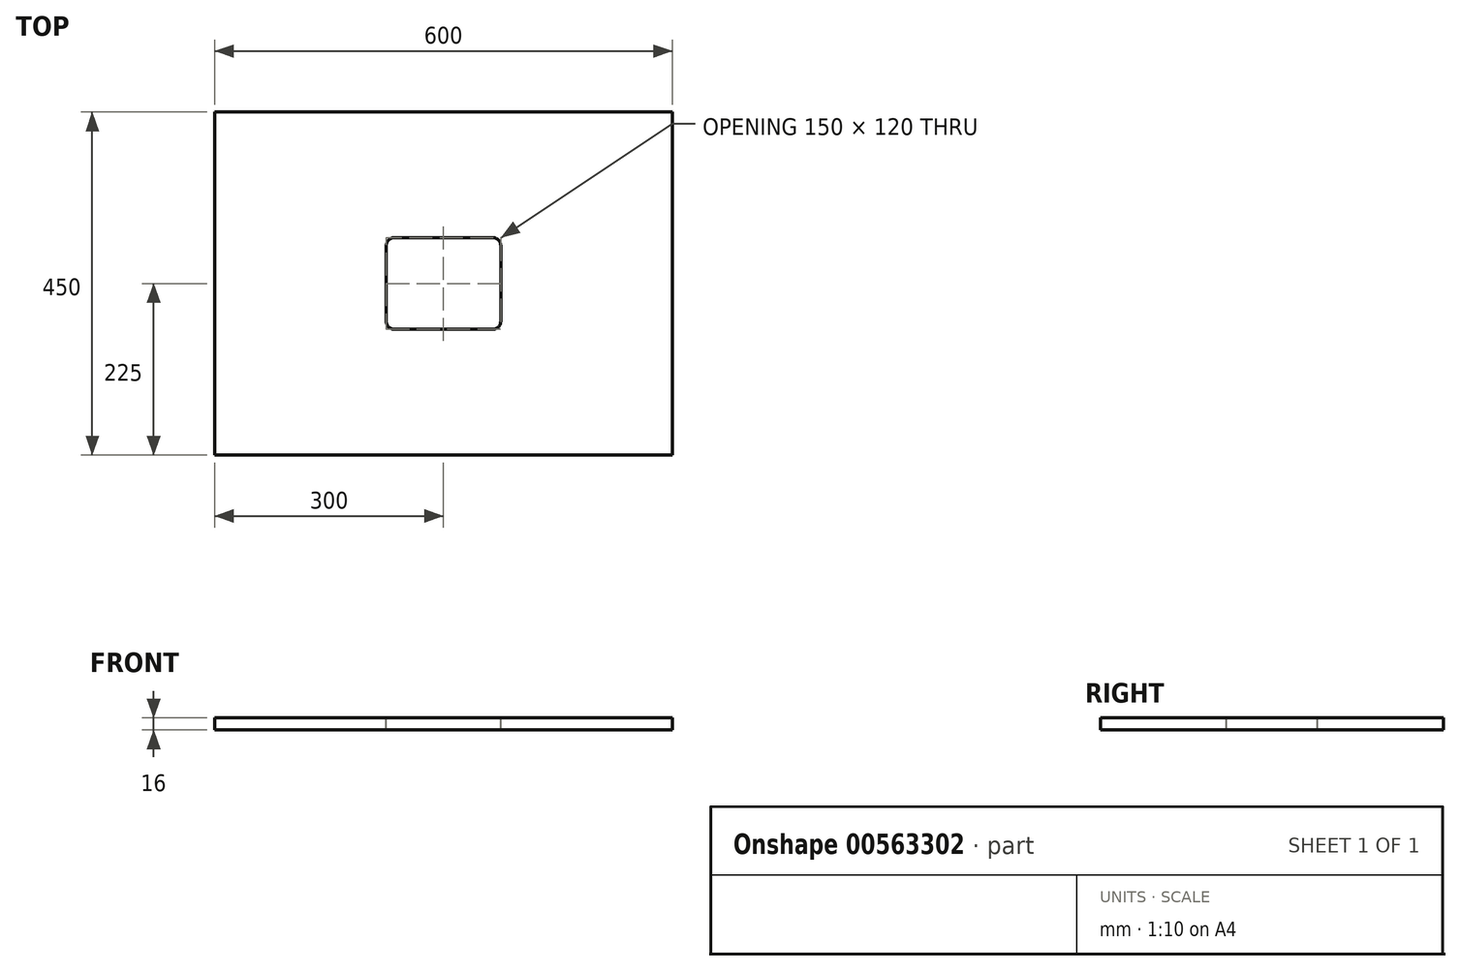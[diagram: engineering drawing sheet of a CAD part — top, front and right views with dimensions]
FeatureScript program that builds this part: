
annotation { "Feature Type Name" : "Feature", "Feature Type Description" : "" }
export const myFeature = defineFeature(function(context is Context, id is Id, definition is map)
    precondition{}
    {
        {
            var Q0;
            Q0=qCreatedBy(makeId("Top.planeOp"),FACE);
            var sketch = newSketch(context, id + "F0", { "sketchPlane" : qUnion([Q0])});
            skLineSegment(sketch, "E0.bottom", {"start": v(300, 225) * mm, "end": v(-300, 225) * mm});
            skLineSegment(sketch, "E0.top", {"start": v(300, -225) * mm, "end": v(-300, -225) * mm});
            skLineSegment(sketch, "E0.left", {"start": v(300, 225) * mm, "end": v(300, -225) * mm});
            skLineSegment(sketch, "E0.right", {"start": v(-300, 225) * mm, "end": v(-300, -225) * mm});
            skPoint(sketch, "E0.middle", {"position": v(0, 0) * mm});
            skSolve(sketch);
        }
        {
            var Q0;
            Q0=makeQuery(id+"F0.imprint","IMPRINT",FACE,{"disambiguationData":[TD([[makeQuery(id+"F0.imprint","IMPRINT",EDGE,{"derivedFrom":sQuery(id+"F0.wireOp",EDGE,"E0.bottom")}),1.0]])]});
            extrude(context, id + "F1", {"entities" : qUnion([Q0]), "depth" : 16 * mm, "offsetDistance" : 25 * mm});
        }
        {
            var Q0;
            Q0=makeQuery(id+"F1.opExtrude","CAP_FACE",FACE,{"disambiguationData":[OSD([sQuery(id+"F0.wireOp",EDGE,"E0.bottom"),sQuery(id+"F0.wireOp",EDGE,"E0.top"),sQuery(id+"F0.wireOp",EDGE,"E0.left"),sQuery(id+"F0.wireOp",EDGE,"E0.right")])],"isStart":false});
            var sketch = newSketch(context, id + "F2", { "sketchPlane" : qUnion([Q0])});
            skLineSegment(sketch, "E1.bottom", {"start": v(75, 60) * mm, "end": v(-75, 60) * mm});
            skLineSegment(sketch, "E1.top", {"start": v(75, -60) * mm, "end": v(-75, -60) * mm});
            skLineSegment(sketch, "E1.left", {"start": v(75, 60) * mm, "end": v(75, -60) * mm});
            skLineSegment(sketch, "E1.right", {"start": v(-75, 60) * mm, "end": v(-75, -60) * mm});
            skPoint(sketch, "E1.middle", {"position": v(0, 0) * mm});
            skSolve(sketch);
        }
        {
            var Q0;
            Q0=makeQuery(id+"F2.imprint","IMPRINT",FACE,{"disambiguationData":[TD([[makeQuery(id+"F2.imprint","IMPRINT",EDGE,{"derivedFrom":sQuery(id+"F2.wireOp",EDGE,"E1.bottom")}),1.0]])]});
            extrude(context, id + "F3", {"entities" : qUnion([Q0]), "operationType" : NewBodyOperationType.REMOVE, "endBound" : BoundingType.THROUGH_ALL, "oppositeDirection" : true, "depth" : 25 * mm, "offsetDistance" : 25 * mm});
        }
        {
            var Q0;
            Q0=makeQuery(id+"F3.boolean.opBoolean","COPY",EDGE,{"derivedFrom":makeQuery(id+"F3.opExtrude","SWEPT_EDGE",EDGE,{"disambiguationData":[OSD([sQuery(id+"F2.wireOp",EDGE,"E1.bottom"),sQuery(id+"F2.wireOp",EDGE,"E1.right")])]})});
            var Q1;
            Q1=makeQuery(id+"F3.boolean.opBoolean","COPY",EDGE,{"derivedFrom":makeQuery(id+"F3.opExtrude","SWEPT_EDGE",EDGE,{"disambiguationData":[OSD([sQuery(id+"F2.wireOp",EDGE,"E1.bottom"),sQuery(id+"F2.wireOp",EDGE,"E1.left")])]})});
            var Q2;
            Q2=makeQuery(id+"F3.boolean.opBoolean","COPY",EDGE,{"derivedFrom":makeQuery(id+"F3.opExtrude","SWEPT_EDGE",EDGE,{"disambiguationData":[OSD([sQuery(id+"F2.wireOp",EDGE,"E1.top"),sQuery(id+"F2.wireOp",EDGE,"E1.left")])]})});
            var Q3;
            Q3=makeQuery(id+"F3.boolean.opBoolean","COPY",EDGE,{"derivedFrom":makeQuery(id+"F3.opExtrude","SWEPT_EDGE",EDGE,{"disambiguationData":[OSD([sQuery(id+"F2.wireOp",EDGE,"E1.top"),sQuery(id+"F2.wireOp",EDGE,"E1.right")])]})});
            fillet(context, id + "F4", {"entities" : qUnion([Q0, Q1, Q2, Q3]), "radius" : 10 * mm, "tangentPropagation" : true, "allowEdgeOverflow" : false});
        }
    });
